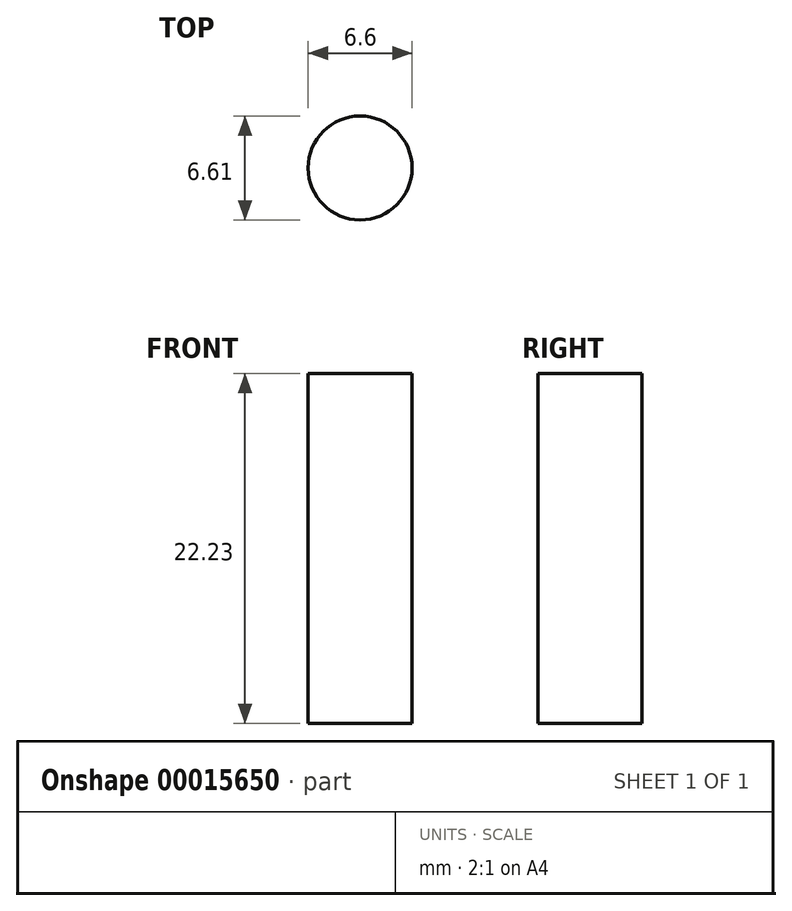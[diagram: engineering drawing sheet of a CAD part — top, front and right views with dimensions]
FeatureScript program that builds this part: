
annotation { "Feature Type Name" : "Feature", "Feature Type Description" : "" }
export const myFeature = defineFeature(function(context is Context, id is Id, definition is map)
    precondition{}
    {
        {
            var Q0;
            Q0=qCreatedBy(makeId("Top.planeOp"),FACE);
            var sketch = newSketch(context, id + "F0", { "sketchPlane" : qUnion([Q0])});
            skCircle(sketch, "E0", {"center": v(-61.61, 43.21) * mm, "radius": 3.3 * mm});
            skSolve(sketch);
        }
        {
            var Q0;
            Q0 = qSketchRegion(id + "F0", true);
            extrude(context, id + "F1", {"entities" : qUnion([Q0]), "depth" : 22.22 * mm});
        }
        {
            var Q0;
            Q0=makeQuery(id+"F1.opExtrude","CAP_FACE",FACE,{"disambiguationData":[OSD([sQuery(id+"F0.wireOp",EDGE,"E0")])],"isStart":false});
            extrude(context, id + "F2", {"entities" : qUnion([Q0]), "operationType" : NewBodyOperationType.ADD, "oppositeDirection" : true, "depth" : 22.22 * mm});
        }
    });
